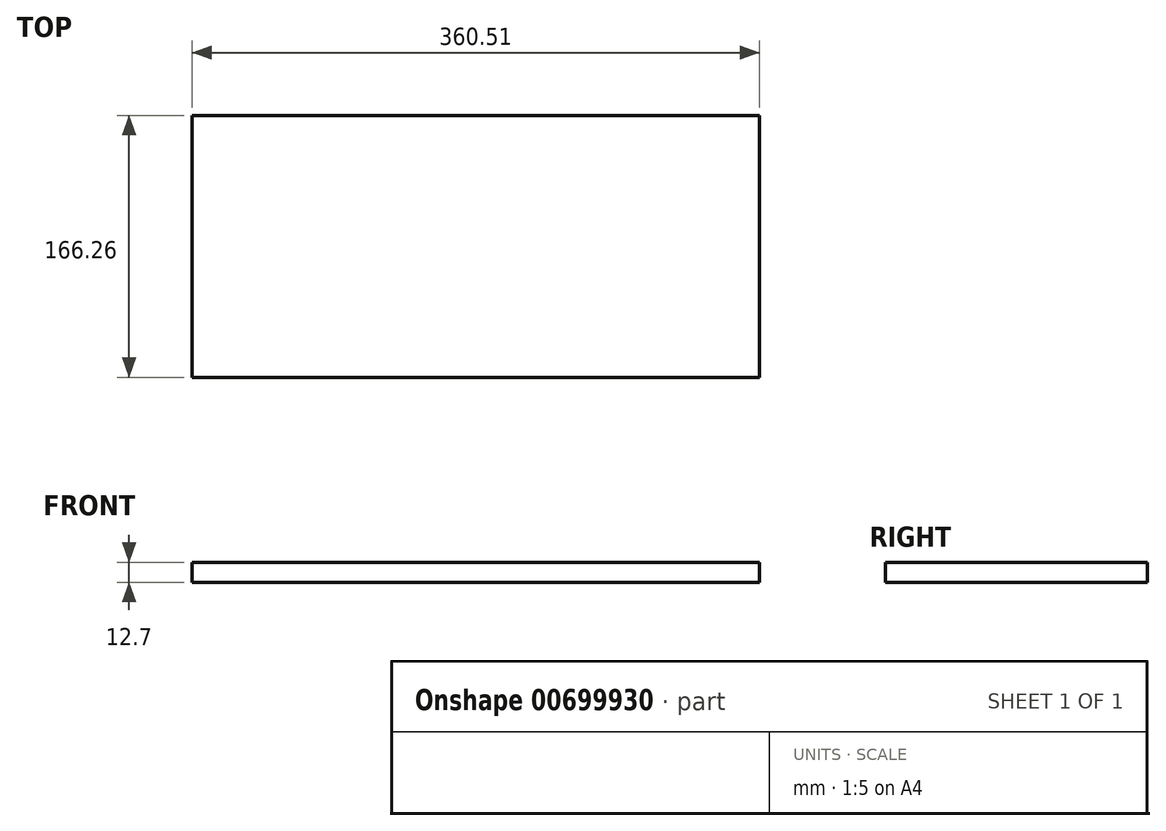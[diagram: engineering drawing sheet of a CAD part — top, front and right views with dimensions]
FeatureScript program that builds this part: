
annotation { "Feature Type Name" : "Feature", "Feature Type Description" : "" }
export const myFeature = defineFeature(function(context is Context, id is Id, definition is map)
    precondition{}
    {
        {
            var Q0;
            Q0=qCreatedBy(makeId("Top.planeOp"),FACE);
            var sketch = newSketch(context, id + "F0", { "sketchPlane" : qUnion([Q0])});
            skLineSegment(sketch, "E0.bottom", {"start": v(-156.6, 92.27) * mm, "end": v(203.92, 92.27) * mm});
            skLineSegment(sketch, "E0.top", {"start": v(-156.6, -73.99) * mm, "end": v(203.92, -73.99) * mm});
            skLineSegment(sketch, "E0.left", {"start": v(-156.6, 92.27) * mm, "end": v(-156.6, -73.99) * mm});
            skLineSegment(sketch, "E0.right", {"start": v(203.92, 92.27) * mm, "end": v(203.92, -73.99) * mm});
            skSolve(sketch);
        }
        {
            var Q0;
            Q0=makeQuery(id+"F0.imprint","IMPRINT",FACE,{"disambiguationData":[TD([[makeQuery(id+"F0.imprint","IMPRINT",EDGE,{"derivedFrom":sQuery(id+"F0.wireOp",EDGE,"E0.bottom")}),-1.0]])]});
            extrude(context, id + "F1", {"entities" : qUnion([Q0]), "depth" : 12.7 * mm, "offsetDistance" : 25.4 * mm});
        }
    });
